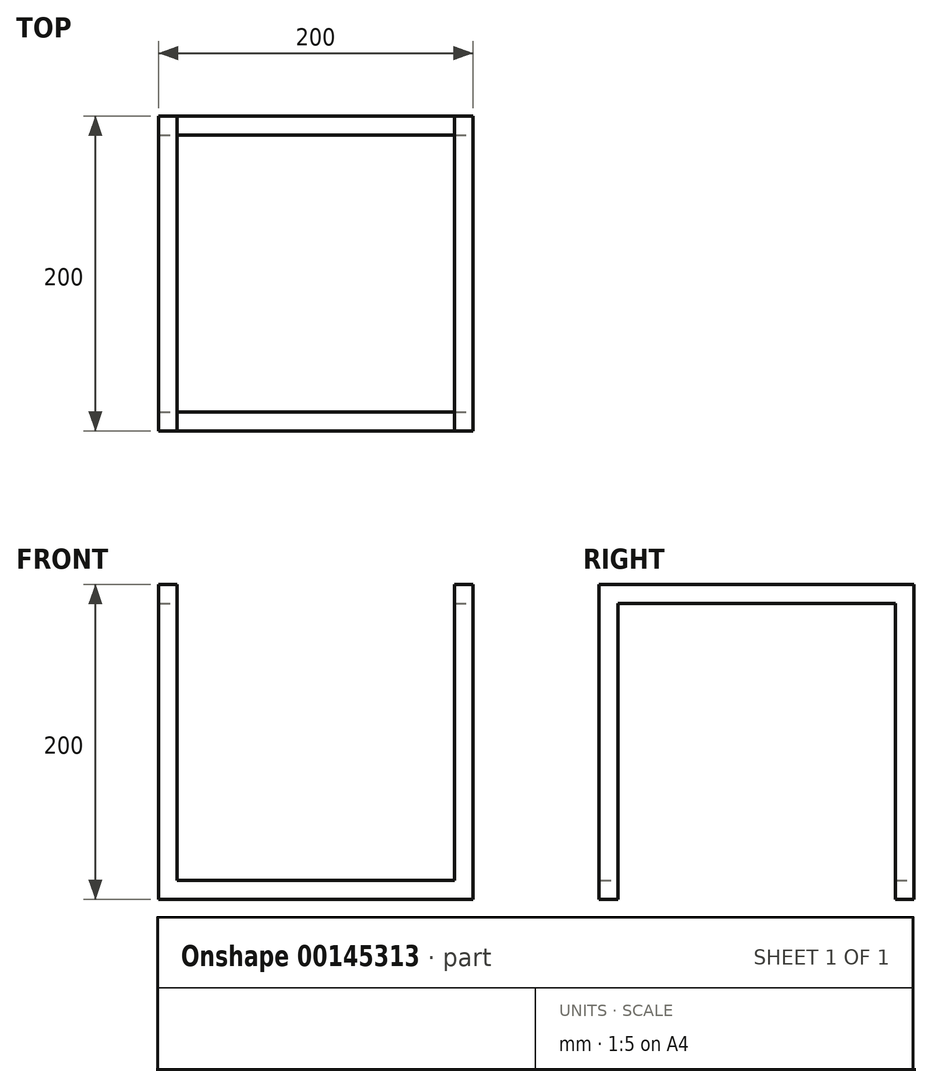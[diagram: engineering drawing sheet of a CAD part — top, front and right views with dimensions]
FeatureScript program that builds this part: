
annotation { "Feature Type Name" : "Feature", "Feature Type Description" : "" }
export const myFeature = defineFeature(function(context is Context, id is Id, definition is map)
    precondition{}
    {
        {
            var Q0;
            Q0=qCreatedBy(makeId("Front.planeOp"),FACE);
            var sketch = newSketch(context, id + "F0", { "sketchPlane" : qUnion([Q0])});
            skLineSegment(sketch, "E0", {"start": v(-100, 0) * mm, "end": v(100, 0) * mm});
            skLineSegment(sketch, "E1", {"start": v(100, 0) * mm, "end": v(100, 200) * mm});
            skLineSegment(sketch, "E2", {"start": v(100, 200) * mm, "end": v(88, 200) * mm});
            skLineSegment(sketch, "E3", {"start": v(88, 200) * mm, "end": v(88, 12) * mm});
            skLineSegment(sketch, "E4", {"start": v(88, 12) * mm, "end": v(-88, 12) * mm});
            skLineSegment(sketch, "E5", {"start": v(-88, 12) * mm, "end": v(-88, 200) * mm});
            skLineSegment(sketch, "E6", {"start": v(-88, 200) * mm, "end": v(-100, 200) * mm});
            skLineSegment(sketch, "E7", {"start": v(-100, 200) * mm, "end": v(-100, 0) * mm});
            skLineSegment(sketch, "E8", {"start": v(-94, 200) * mm, "end": v(-94, 6) * mm});
            skLineSegment(sketch, "E9", {"start": v(-94, 6) * mm, "end": v(94, 6) * mm});
            skLineSegment(sketch, "E10", {"start": v(94, 6) * mm, "end": v(94, 200) * mm});
            skSolve(sketch);
        }
        {
            var Q0;
            {var subQ2=sQuery(id+"F0.wireOp",EDGE,"E3");Q0=makeQuery(id+"F0.imprint","IMPRINT",FACE,{"disambiguationData":[TD([[makeQuery(id+"F0.imprint","IMPRINT",EDGE,{"derivedFrom":subQ2}),1.0]])]});}
            var Q1;
            Q1=makeQuery(id+"F0.imprint","IMPRINT",FACE,{"disambiguationData":[TD([[makeQuery(id+"F0.imprint","IMPRINT",EDGE,{"derivedFrom":sQuery(id+"F0.wireOp",EDGE,"E0")}),1.0]])]});
            extrude(context, id + "F1", {"entities" : qUnion([Q0, Q1]), "endBound" : BoundingType.SYMMETRIC, "depth" : 200 * mm});
        }
        {
            var Q0;
            Q0=makeQuery(id+"F1.opExtrude","SWEPT_FACE",FACE,{"disambiguationData":[OSD([sQuery(id+"F0.wireOp",EDGE,"E1")])]});
            var sketch = newSketch(context, id + "F2", { "sketchPlane" : qUnion([Q0])});
            skLineSegment(sketch, "E11.bottom", {"start": v(-88, 0) * mm, "end": v(88, 0) * mm});
            skLineSegment(sketch, "E11.top", {"start": v(-88, 188) * mm, "end": v(88, 188) * mm});
            skLineSegment(sketch, "E11.left", {"start": v(-88, 0) * mm, "end": v(-88, 188) * mm});
            skLineSegment(sketch, "E11.right", {"start": v(88, 0) * mm, "end": v(88, 188) * mm});
            skSolve(sketch);
        }
        {
            var Q0;
            Q0 = qSketchRegion(id + "F2", true);
            extrude(context, id + "F3", {"entities" : qUnion([Q0]), "operationType" : NewBodyOperationType.REMOVE, "endBound" : BoundingType.THROUGH_ALL, "oppositeDirection" : true, "depth" : 25 * mm});
        }
    });
